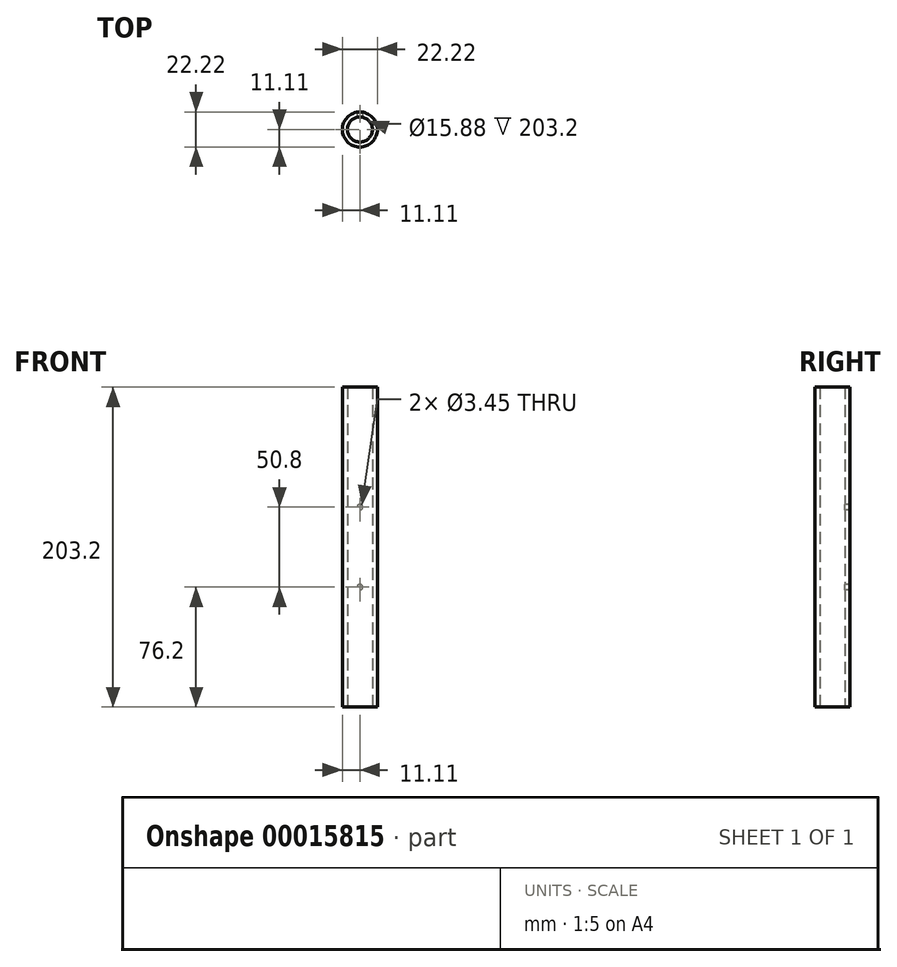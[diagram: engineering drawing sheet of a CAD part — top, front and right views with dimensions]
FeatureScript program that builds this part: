
annotation { "Feature Type Name" : "Feature", "Feature Type Description" : "" }
export const myFeature = defineFeature(function(context is Context, id is Id, definition is map)
    precondition{}
    {
        {
            var Q0;
            Q0=qCreatedBy(makeId("Top.planeOp"),FACE);
            var sketch = newSketch(context, id + "F0", { "sketchPlane" : qUnion([Q0])});
            skCircle(sketch, "E0", {"center": v(0, 0) * mm, "radius": 7.94 * mm});
            skCircle(sketch, "E1", {"center": v(0, 0) * mm, "radius": 11.11 * mm});
            skSolve(sketch);
        }
        {
            var Q0;
            Q0=qSketchRegion(id+"F0",true);
            extrude(context, id + "F1", {"entities" : qUnion([Q0]), "depth" : 203.2 * mm});
        }
        {
            var Q0;
            Q0=qCreatedBy(makeId("Front.planeOp"),FACE);
            var sketch = newSketch(context, id + "F2", { "sketchPlane" : qUnion([Q0])});
            skLineSegment(sketch, "E2", {"start": v(0, 203.2) * mm, "end": v(0, 127) * mm, "construction": true});
            skLineSegment(sketch, "E3", {"start": v(0, 127) * mm, "end": v(0, 76.2) * mm, "construction": true});
            skLineSegment(sketch, "E4", {"start": v(0, 76.2) * mm, "end": v(0, 0) * mm, "construction": true});
            skCircle(sketch, "E5", {"center": v(0, 127) * mm, "radius": 1.73 * mm});
            skCircle(sketch, "E6", {"center": v(0, 76.2) * mm, "radius": 1.73 * mm});
            skSolve(sketch);
        }
        {
            var Q0;
            Q0 = qSketchRegion(id + "F2", true);
            var Q1;
            Q1=makeQuery(id+"F1.opExtrude","SWEPT_FACE",FACE,{"disambiguationData":[OSD([sQuery(id+"F0.wireOp",EDGE,"E1")])]});
            extrude(context, id + "F3", {"entities" : qUnion([Q0]), "operationType" : NewBodyOperationType.REMOVE, "endBound" : BoundingType.UP_TO_SURFACE, "oppositeDirection" : true, "endBoundEntityFace" : qUnion([Q1]), "depth" : 25.4 * mm});
        }
    });
